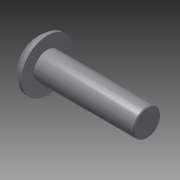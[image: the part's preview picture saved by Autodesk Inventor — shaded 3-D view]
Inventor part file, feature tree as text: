
AUTODESK INVENTOR PART (.ipt)
format: ipt  version: 2015 (Build 190159000, 159)  size: 137,216 bytes
history: native  units: in
note: dims shown in document units (in); Inventor stores cm internally (conversion verified against a paired STEP export)
features: other x2, extrude x1, chamfer x1, imported_body x1, sketch x1
ambient origin geometry x8: Origin, YZ Plane, XZ Plane, XY Plane, X Axis, Y Axis, Z Axis, Center Point
bodies: Body1 (feature_tree)
feature tree (6):
  parser-record x1  (decoder bookkeeping rows leaked as tree rows — omitted from the tree; the rows remain in map.json)
  other  "Motor Bolt"
  extrude  "thread length"  Depth=0.5in TaperAngle=0.0deg
  chamfer  "thread chamfer"  Distance=0.004in Angle=45.0deg
  imported_body  "Base1"
  sketch  "Sketch1"  dims[d0=0.135in d1=0.5in d2=0.0in d3=0.004in d4=0.125in d5=45.0deg d7=0.0in d8=0.0in]
